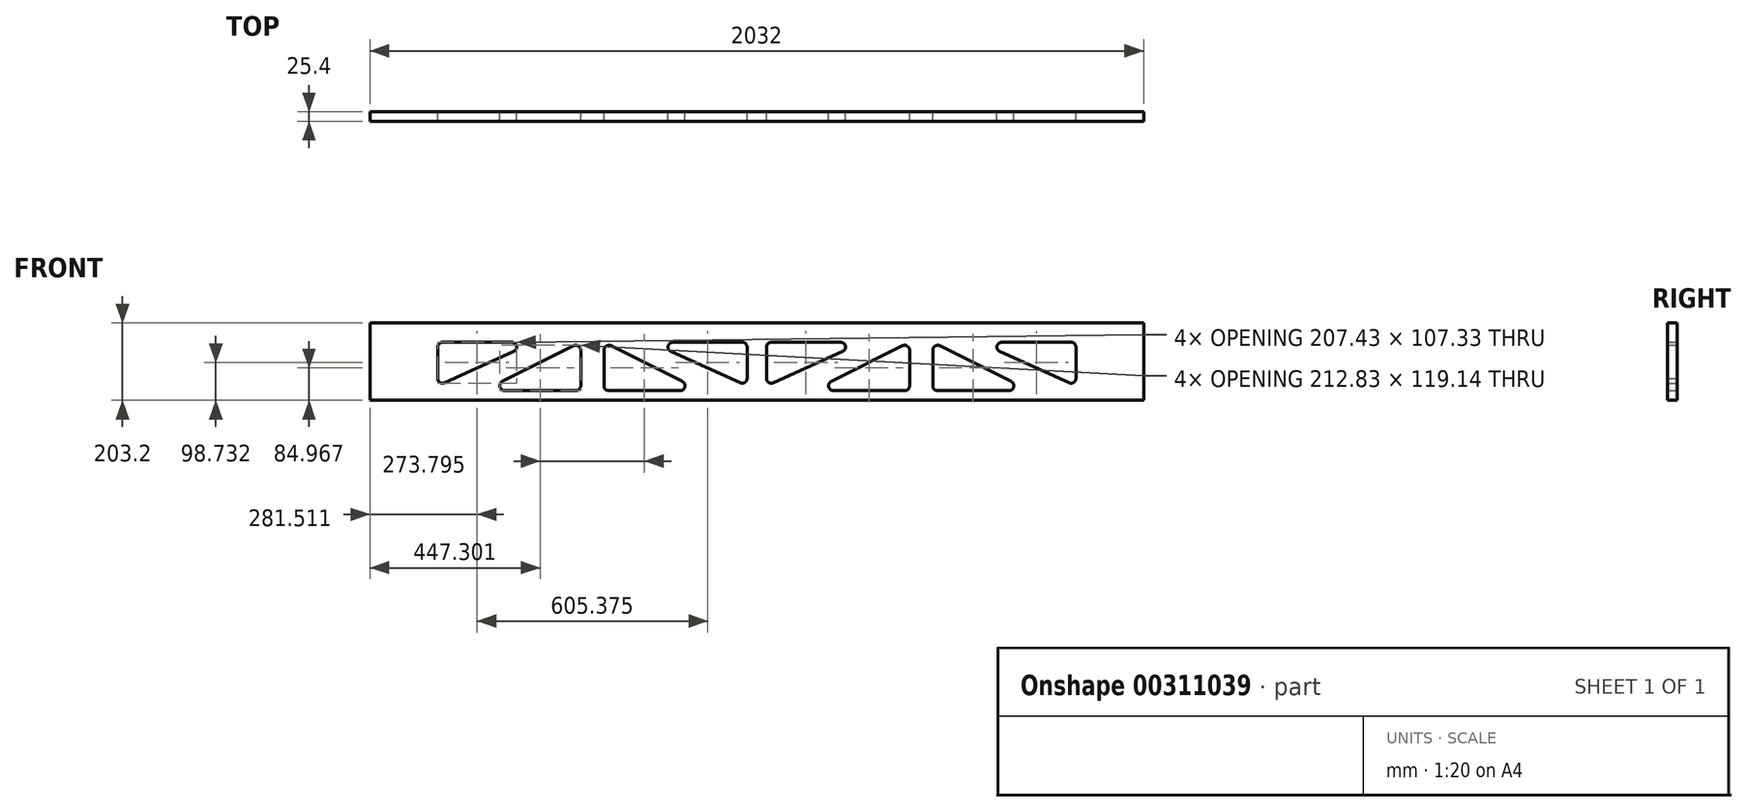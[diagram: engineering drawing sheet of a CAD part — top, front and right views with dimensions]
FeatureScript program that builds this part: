
annotation { "Feature Type Name" : "Feature", "Feature Type Description" : "" }
export const myFeature = defineFeature(function(context is Context, id is Id, definition is map)
    precondition{}
    {
        {
            var Q0;
            Q0=qCreatedBy(makeId("Front.planeOp"),FACE);
            var sketch = newSketch(context, id + "F0", { "sketchPlane" : qUnion([Q0])});
            skLineSegment(sketch, "E0.bottom", {"start": v(-1108.64, 137.78) * mm, "end": v(923.36, 137.78) * mm});
            skLineSegment(sketch, "E0.top", {"start": v(-1108.64, -65.42) * mm, "end": v(923.36, -65.42) * mm});
            skLineSegment(sketch, "E0.left", {"start": v(-1108.64, 137.78) * mm, "end": v(-1108.64, -65.42) * mm});
            skLineSegment(sketch, "E0.right", {"start": v(923.36, 137.78) * mm, "end": v(923.36, -65.42) * mm});
            skLineSegment(sketch, "E1", {"start": v(-92.64, 137.78) * mm, "end": v(-92.64, -65.42) * mm, "construction": true});
            skLineSegment(sketch, "E2", {"start": v(-67.24, 74.28) * mm, "end": v(-67.24, -8.6) * mm});
            skLineSegment(sketch, "E3", {"start": v(-54.54, 86.98) * mm, "end": v(127.59, 86.98) * mm});
            skLineSegment(sketch, "E4", {"start": v(132.8, 62.7) * mm, "end": v(-49.33, -19.26) * mm});
            skLineSegment(sketch, "E5", {"start": v(308.68, 66.43) * mm, "end": v(308.68, -27.32) * mm});
            skLineSegment(sketch, "E6", {"start": v(295.98, -40.02) * mm, "end": v(108.48, -40.02) * mm});
            skLineSegment(sketch, "E7", {"start": v(102.8, -15.96) * mm, "end": v(290.3, 77.79) * mm});
            skPoint(sketch, "E8.visualSharp", {"position": v(-67.24, 86.98) * mm});
            skArc(sketch, "E8.filletArc", {"start": v(-54.54, 86.98) * mm, "mid": v(-63.52, 83.26) * mm, "end": v(-67.24, 74.28) * mm});
            skPoint(sketch, "E9.visualSharp", {"position": v(-67.24, -27.32) * mm});
            skArc(sketch, "E9.filletArc", {"start": v(-67.23, -8.22) * mm, "mid": v(-61.21, -18.49) * mm, "end": v(-49.33, -19.26) * mm});
            skPoint(sketch, "E10.visualSharp", {"position": v(186.76, 86.98) * mm});
            skArc(sketch, "E10.filletArc", {"start": v(132.8, 62.7) * mm, "mid": v(140, 76.94) * mm, "end": v(127.59, 86.98) * mm});
            skPoint(sketch, "E11.visualSharp", {"position": v(308.68, 86.98) * mm});
            skArc(sketch, "E11.filletArc", {"start": v(308.68, 82.49) * mm, "mid": v(307.36, 84.85) * mm, "end": v(304.66, 84.97) * mm});
            skPoint(sketch, "E12.visualSharp", {"position": v(308.68, -40.02) * mm});
            skPoint(sketch, "E13.visualSharp", {"position": v(54.68, -40.02) * mm});
            skLineSegment(sketch, "E14", {"start": v(339.16, 137.78) * mm, "end": v(339.16, -65.42) * mm, "construction": true});
            skPoint(sketch, "E15.filletArc.end.orphan", {"position": v(-64.23, -25.97) * mm});
            skPoint(sketch, "E16.end.orphan", {"position": v(-67.24, -36.72) * mm});
            skLineSegment(sketch, "E17", {"start": v(-67.24, -8.6) * mm, "end": v(-67.23, -8.22) * mm});
            skPoint(sketch, "E13.filletArc.end.orphan", {"position": v(36.75, -40.02) * mm});
            skPoint(sketch, "E13.filletArc.start.orphan", {"position": v(38.64, -48.04) * mm});
            skArc(sketch, "E18.filletArc", {"start": v(102.8, -15.96) * mm, "mid": v(96.12, -30.24) * mm, "end": v(108.48, -40.02) * mm});
            skPoint(sketch, "E19.newPointA", {"position": v(304.66, 84.97) * mm});
            skPoint(sketch, "E19.newPointB", {"position": v(308.68, 82.49) * mm});
            skArc(sketch, "E19.filletArc", {"start": v(308.68, 66.43) * mm, "mid": v(302.65, 77.23) * mm, "end": v(290.3, 77.79) * mm});
            skPoint(sketch, "E20.newPointA", {"position": v(302.33, -40.02) * mm});
            skPoint(sketch, "E20.newPointB", {"position": v(308.68, -33.67) * mm});
            skArc(sketch, "E20.filletArc", {"start": v(295.98, -40.02) * mm, "mid": v(304.96, -36.3) * mm, "end": v(308.68, -27.32) * mm});
            skLineSegment(sketch, "E21.MirrorCS", {"start": v(732.86, 86.98) * mm, "end": v(550.73, 86.98) * mm});
            skArc(sketch, "E22.MirrorCS", {"start": v(545.52, 62.7) * mm, "mid": v(538.31, 76.94) * mm, "end": v(550.73, 86.98) * mm});
            skLineSegment(sketch, "E23.MirrorCS", {"start": v(545.52, 62.7) * mm, "end": v(727.65, -19.26) * mm});
            skArc(sketch, "E24.MirrorCS", {"start": v(745.55, -8.22) * mm, "mid": v(739.53, -18.49) * mm, "end": v(727.65, -19.26) * mm});
            skLineSegment(sketch, "E25.MirrorCS", {"start": v(745.56, 74.28) * mm, "end": v(745.56, -8.6) * mm});
            skLineSegment(sketch, "E26.MirrorCS", {"start": v(745.56, -8.6) * mm, "end": v(745.55, -8.22) * mm});
            skLineSegment(sketch, "E27.MirrorCS", {"start": v(575.52, -15.96) * mm, "end": v(388.02, 77.79) * mm});
            skArc(sketch, "E28.MirrorCS", {"start": v(575.52, -15.96) * mm, "mid": v(582.2, -30.24) * mm, "end": v(569.84, -40.02) * mm});
            skLineSegment(sketch, "E29.MirrorCS", {"start": v(382.34, -40.02) * mm, "end": v(569.84, -40.02) * mm});
            skLineSegment(sketch, "E30.MirrorCS", {"start": v(369.64, 66.43) * mm, "end": v(369.64, -27.32) * mm});
            skArc(sketch, "E31.MirrorCS", {"start": v(369.64, 66.43) * mm, "mid": v(375.66, 77.23) * mm, "end": v(388.02, 77.79) * mm});
            skArc(sketch, "E32.MirrorCS", {"start": v(382.34, -40.02) * mm, "mid": v(373.36, -36.3) * mm, "end": v(369.64, -27.32) * mm});
            skArc(sketch, "E33.MirrorCS", {"start": v(732.86, 86.98) * mm, "mid": v(741.84, 83.26) * mm, "end": v(745.56, 74.28) * mm});
            skArc(sketch, "E34.MirrorCS", {"start": v(-493.96, 82.49) * mm, "mid": v(-492.65, 84.85) * mm, "end": v(-489.95, 84.97) * mm});
            skLineSegment(sketch, "E35.MirrorCS", {"start": v(-118.04, -8.6) * mm, "end": v(-118.05, -8.22) * mm});
            skArc(sketch, "E36.MirrorCS", {"start": v(-567.62, -40.02) * mm, "mid": v(-558.64, -36.3) * mm, "end": v(-554.92, -27.32) * mm});
            skLineSegment(sketch, "E37.MirrorCS", {"start": v(-930.84, -8.6) * mm, "end": v(-930.83, -8.22) * mm});
            skArc(sketch, "E38.MirrorCS", {"start": v(-918.14, 86.98) * mm, "mid": v(-927.12, 83.26) * mm, "end": v(-930.84, 74.28) * mm});
            skArc(sketch, "E39.MirrorCS", {"start": v(-493.96, 66.43) * mm, "mid": v(-487.94, 77.23) * mm, "end": v(-475.58, 77.79) * mm});
            skArc(sketch, "E40.MirrorCS", {"start": v(-118.05, -8.22) * mm, "mid": v(-124.07, -18.49) * mm, "end": v(-135.95, -19.26) * mm});
            skArc(sketch, "E41.MirrorCS", {"start": v(-481.26, -40.02) * mm, "mid": v(-490.24, -36.3) * mm, "end": v(-493.96, -27.32) * mm});
            skArc(sketch, "E42.MirrorCS", {"start": v(-130.74, 86.98) * mm, "mid": v(-121.76, 83.26) * mm, "end": v(-118.04, 74.28) * mm});
            skArc(sketch, "E43.MirrorCS", {"start": v(-288.08, -15.96) * mm, "mid": v(-281.4, -30.24) * mm, "end": v(-293.76, -40.02) * mm});
            skPoint(sketch, "E44.MirrorP", {"position": v(-118.04, -27.32) * mm});
            skPoint(sketch, "E45.MirrorP", {"position": v(-239.96, -40.02) * mm});
            skLineSegment(sketch, "E46.MirrorCS", {"start": v(-481.26, -40.02) * mm, "end": v(-293.76, -40.02) * mm});
            skLineSegment(sketch, "E47.MirrorCS", {"start": v(-493.96, 66.43) * mm, "end": v(-493.96, -27.32) * mm});
            skLineSegment(sketch, "E48.MirrorCS", {"start": v(-318.08, 62.7) * mm, "end": v(-135.95, -19.26) * mm});
            skLineSegment(sketch, "E49.MirrorCS", {"start": v(-130.74, 86.98) * mm, "end": v(-312.87, 86.98) * mm});
            skLineSegment(sketch, "E50.MirrorCS", {"start": v(-118.04, 74.28) * mm, "end": v(-118.04, -8.6) * mm});
            skPoint(sketch, "E51.MirrorP", {"position": v(-223.93, -48.04) * mm});
            skPoint(sketch, "E52.MirrorP", {"position": v(-493.96, -33.67) * mm});
            skArc(sketch, "E53.MirrorCS", {"start": v(-760.8, -15.96) * mm, "mid": v(-767.48, -30.24) * mm, "end": v(-755.12, -40.02) * mm});
            skLineSegment(sketch, "E54.MirrorCS", {"start": v(-288.08, -15.96) * mm, "end": v(-475.58, 77.79) * mm});
            skPoint(sketch, "E55.MirrorP", {"position": v(-222.03, -40.02) * mm});
            skPoint(sketch, "E56.MirrorP", {"position": v(-487.61, -40.02) * mm});
            skLineSegment(sketch, "E57.MirrorCS", {"start": v(-567.62, -40.02) * mm, "end": v(-755.12, -40.02) * mm});
            skArc(sketch, "E58.MirrorCS", {"start": v(-554.92, 66.43) * mm, "mid": v(-560.95, 77.23) * mm, "end": v(-573.3, 77.79) * mm});
            skPoint(sketch, "E59.MirrorP", {"position": v(-372.04, 86.98) * mm});
            skPoint(sketch, "E60.MirrorP", {"position": v(-493.96, 86.98) * mm});
            skPoint(sketch, "E61.MirrorP", {"position": v(-118.04, 86.98) * mm});
            skPoint(sketch, "E62.MirrorP", {"position": v(-489.95, 84.97) * mm});
            skArc(sketch, "E63.MirrorCS", {"start": v(-318.08, 62.7) * mm, "mid": v(-325.29, 76.94) * mm, "end": v(-312.87, 86.98) * mm});
            skLineSegment(sketch, "E64.MirrorCS", {"start": v(-730.8, 62.7) * mm, "end": v(-912.93, -19.26) * mm});
            skPoint(sketch, "E65.MirrorP", {"position": v(-118.04, -36.72) * mm});
            skPoint(sketch, "E66.MirrorP", {"position": v(-493.96, -40.02) * mm});
            skLineSegment(sketch, "E67.MirrorCS", {"start": v(-918.14, 86.98) * mm, "end": v(-736.01, 86.98) * mm});
            skLineSegment(sketch, "E68.MirrorCS", {"start": v(-760.8, -15.96) * mm, "end": v(-573.3, 77.79) * mm});
            skPoint(sketch, "E69.MirrorP", {"position": v(-121.05, -25.97) * mm});
            skArc(sketch, "E70.MirrorCS", {"start": v(-730.8, 62.7) * mm, "mid": v(-723.6, 76.94) * mm, "end": v(-736.01, 86.98) * mm});
            skArc(sketch, "E71.MirrorCS", {"start": v(-930.83, -8.22) * mm, "mid": v(-924.81, -18.49) * mm, "end": v(-912.93, -19.26) * mm});
            skLineSegment(sketch, "E72.MirrorCS", {"start": v(-930.84, 74.28) * mm, "end": v(-930.84, -8.6) * mm});
            skPoint(sketch, "E73.MirrorP", {"position": v(-493.96, 82.49) * mm});
            skLineSegment(sketch, "E74.MirrorCS", {"start": v(-554.92, 66.43) * mm, "end": v(-554.92, -27.32) * mm});
            skSolve(sketch);
        }
        {
            var Q0;
            Q0=makeQuery(id+"F0.imprint","IMPRINT",FACE,{"disambiguationData":[TD([[makeQuery(id+"F0.imprint","IMPRINT",EDGE,{"derivedFrom":sQuery(id+"F0.wireOp",EDGE,"E0.bottom")}),-1.0]])]});
            extrude(context, id + "F1", {"entities" : qUnion([Q0]), "depth" : 25.4 * mm});
        }
    });
